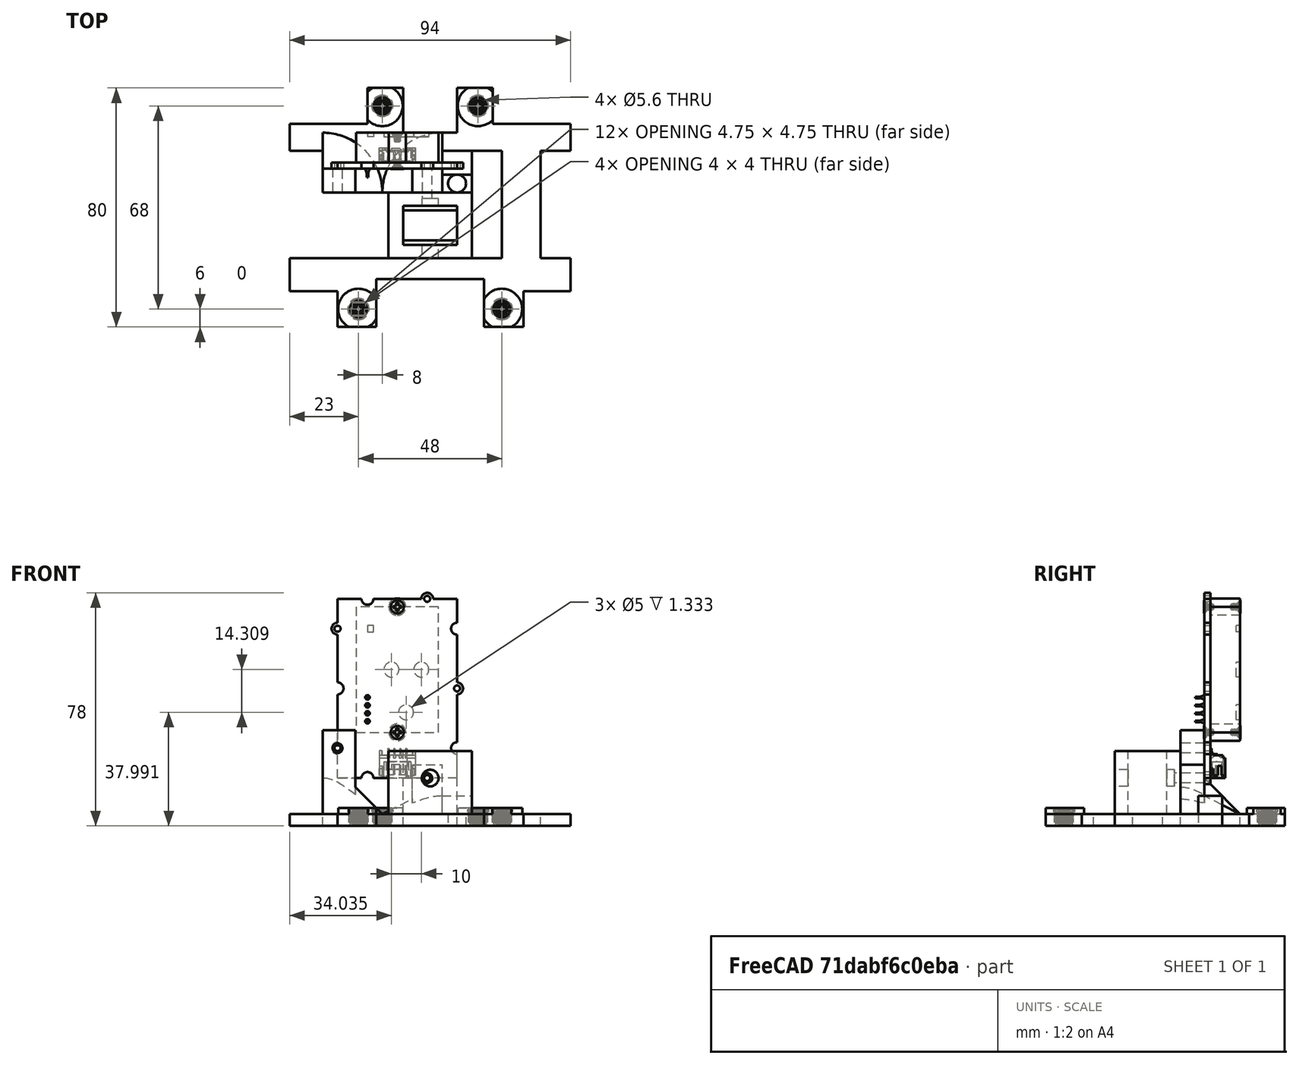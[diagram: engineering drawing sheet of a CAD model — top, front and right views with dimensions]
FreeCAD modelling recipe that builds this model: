
FCSTD DOCUMENT  (FreeCAD 0.20R29410 (Git))
Label: spin07132022
License: All rights reserved
LicenseURL: http://en.wikipedia.org/wiki/All_rights_reserved
objects: Part::Box×25, Part::Cylinder×18, Part::MultiFuse×16, Part::Cut×5, Part::Feature×5, Part::Cone×2
note: 71 computed .brp shape members not serialized (recipe doc carries the construction recipe); baked Part::Feature solids carry a one-line shape summary decoded from their .brp

FEATURE [Part::Cylinder] Cylinder103  label="Cylinder107"
  Angle = 360
  AttacherType = Attacher::AttachEngine3D
  FirstAngle = 0
  Height = 10
  Placement = pos=(63,3,0) rot=(0,0,1;0rad)
  Radius = 2.25
  SecondAngle = 0
FEATURE [Part::Box] Box064  label="base005"
  AttacherType = Attacher::AttachEngine3D
  Height = 4
  Length = 26
  Placement = pos=(-10.25,68,0) rot=(0,0,1;0rad)
  Width = 12
FEATURE [Part::Box] Box060  label="base001"
  AttacherType = Attacher::AttachEngine3D
  Height = 4
  Length = 94
  Width = 80
FEATURE [Part::Box] Box061  label="base002"
  AttacherType = Attacher::AttachEngine3D
  Height = 4
  Length = 26
  Width = 12
FEATURE [Part::Box] Box062  label="base003"
  AttacherType = Attacher::AttachEngine3D
  Height = 4
  Length = 26
  Placement = pos=(68,0,0) rot=(0,0,1;0rad)
  Width = 12
FEATURE [Part::Cylinder] Cylinder104  label="Cylinder103"
  Angle = 360
  AttacherType = Attacher::AttachEngine3D
  FirstAngle = 0
  Height = 10
  Placement = pos=(71,71,0) rot=(0,0,1;0rad)
  Radius = 2.25
  SecondAngle = 0
FEATURE [Part::Cylinder] Cylinder106  label="Cylinder104"
  Angle = 360
  AttacherType = Attacher::AttachEngine3D
  FirstAngle = 0
  Height = 10
  Placement = pos=(23,71,0) rot=(0,0,1;0rad)
  Radius = 2
  SecondAngle = 0
FEATURE [Part::Cylinder] Cylinder105  label="Cylinder108"
  Angle = 360
  AttacherType = Attacher::AttachEngine3D
  FirstAngle = 0
  Height = 10
  Placement = pos=(31,3,0) rot=(0,0,1;0rad)
  Radius = 2.25
  SecondAngle = 0
FEATURE [Part::Box] Box081  label="Cube039"
  AttacherType = Attacher::AttachEngine3D
  Height = 10
  Length = 10
  Placement = pos=(74,27,140) rot=(0,0,1;0rad)
  Width = 36
FEATURE [Part::Box] Box082  label="Cube040"
  AttacherType = Attacher::AttachEngine3D
  Height = 10
  Length = 36
  Placement = pos=(42,1,140) rot=(0,0,1;0rad)
  Width = 19
FEATURE [Part::Box] Box073  label="baseSpineCut"
  AttacherType = Attacher::AttachEngine3D
  Height = 25
  Length = 18
  Placement = pos=(51,33,140) rot=(0,0,1;0rad)
  Width = 10
FEATURE [Part::Cylinder] Cylinder107  label="Cylinder109"
  Angle = 360
  AttacherType = Attacher::AttachEngine3D
  FirstAngle = 0
  Height = 10
  Radius = 1
  SecondAngle = 0
FEATURE [Part::MultiFuse] Fusion123  label="screwIns001"
  Placement = pos=(0,3,0) rot=(0,0,1;0rad)
  Shapes = -> [Cylinder105,Cylinder107,Cylinder103,Cylinder104,Cylinder106]
FEATURE [Part::Box] Box080  label="Cube038"
  AttacherType = Attacher::AttachEngine3D
  Height = 10
  Length = 33
  Placement = pos=(13,27,140) rot=(0,0,1;0rad)
  Width = 22
FEATURE [Part::Box] Box063  label="base004"
  AttacherType = Attacher::AttachEngine3D
  Height = 4
  Length = 26
  Placement = pos=(78,68,0) rot=(0,0,1;0rad)
  Width = 12
FEATURE [Part::MultiFuse] Fusion122
  Shapes = -> [Box064,Box063,Box061,Box062]
FEATURE [Part::Cut] Cut019  label="baseNew"
  Base = -> Box060
  Tool = -> Fusion122
FEATURE [Part::Cut] Cut020  label="baseNew001"
  Base = -> Cut019
  Placement = pos=(107,84,140) rot=(0,0,1;3.14159rad)
  Tool = -> Fusion123
FEATURE [Part::Box] Box083  label="Cube041"
  AttacherType = Attacher::AttachEngine3D
  Height = 25
  Length = 18
  Placement = pos=(51,31.5,144) rot=(0,0,1;0rad)
  Width = 13
FEATURE [Part::Box] Box084  label="Cube042"
  AttacherType = Attacher::AttachEngine3D
  Height = 51
  Length = 50
  Placement = pos=(24,49,140) rot=(0,0,1;0rad)
  Width = 8
FEATURE [Part::Box] Box085  label="Cube043"
  AttacherType = Attacher::AttachEngine3D
  Height = 10
  Length = 15
  Placement = pos=(69,69,140) rot=(0,0,1;1.5708rad)
  Width = 18
FEATURE [Part::Box] Box086  label="baseSpineIn"
  AttacherType = Attacher::AttachEngine3D
  Height = 25
  Length = 28
  Placement = pos=(46,27,140) rot=(0,0,1;0rad)
  Width = 22
FEATURE [Part::Cylinder] Cylinder
  Angle = 360
  AttacherType = Attacher::AttachEngine3D
  FirstAngle = 0
  Height = 50
  Placement = pos=(60,-3,156) rot=(-1,0,0;1.5708rad)
  Radius = 2.8
  SecondAngle = 0
FEATURE [Part::Feature] Feature  label="Seed Grove SCD30"
  Placement = pos=(29,59,156) rot=(0.707107,0,0.707107;3.14159rad)
  shape: bbox 44 x 15.1 x 64 mm, 422 faces, 13 solids (baked)
FEATURE [Part::Cylinder] Cylinder108  label="Cylinder110"
  Angle = 360
  AttacherType = Attacher::AttachEngine3D
  FirstAngle = 0
  Height = 50
  Placement = pos=(80,17,186) rot=(-1,0,0;1.5708rad)
  Radius = 1.65
  SecondAngle = 0
FEATURE [Part::Cylinder] Cylinder109  label="Cylinder111"
  Angle = 360
  AttacherType = Attacher::AttachEngine3D
  FirstAngle = 0
  Height = 50
  Placement = pos=(40,17,166) rot=(-1,0,0;1.5708rad)
  Radius = 1.65
  SecondAngle = 0
FEATURE [Part::Cylinder] Cylinder110  label="Cylinder112"
  Angle = 360
  AttacherType = Attacher::AttachEngine3D
  FirstAngle = 0
  Height = 50
  Placement = pos=(70,17,156) rot=(-1,0,0;1.5708rad)
  Radius = 1.65
  SecondAngle = 0
FEATURE [Part::MultiFuse] Fusion  label="m2Cuts"
  Placement = pos=(-11,30,0) rot=(0,0,1;0rad)
  Shapes = -> [Cylinder108,Cylinder109,Cylinder110]
FEATURE [Part::Box] Box087  label="Cube044"
  AttacherType = Attacher::AttachEngine3D
  Height = 51
  Length = 50
  Placement = pos=(13,49,172) rot=(0,0,1;0rad)
  Width = 8
FEATURE [Part::Box] Box088  label="Cube045"
  AttacherType = Attacher::AttachEngine3D
  Height = 51
  Length = 19
  Placement = pos=(35,49,144) rot=(0,0,1;0rad)
  Width = 8
FEATURE [Part::MultiFuse] Fusion124  label="base"
  Shapes = -> [Cut020,Box084,Box086]
FEATURE [Part::MultiFuse] Fusion125  label="cuts"
  Shapes = -> [Box087,Box088,Fusion,Box085,Box080,Box083,Box082,Box081,Box073,Cylinder]
FEATURE [Part::Box] Box089  label="Cube046"
  AttacherType = Attacher::AttachEngine3D
  Height = 10
  Length = 11
  Placement = pos=(13,57,140) rot=(0,0,1;0rad)
  Width = 6
FEATURE [Part::Feature] Solid  label="m4HeatSet"
  Placement = pos=(36,10,140) rot=(1,0,0;1.5708rad)
  shape: bbox 7.1 x 7.1 x 6.065 mm, 234 faces (baked)
FEATURE [Part::Feature] Solid001  label="m4HeatSet001"
  Placement = pos=(84,10,140) rot=(1,0,0;1.5708rad)
  shape: bbox 7.1 x 7.1 x 6.065 mm, 234 faces (baked)
FEATURE [Part::Feature] Solid002  label="m4HeatSet002"
  Placement = pos=(44,78,140) rot=(1,0,0;1.5708rad)
  shape: bbox 7.1 x 7.1 x 6.065 mm, 234 faces (baked)
FEATURE [Part::Feature] Solid003  label="m4HeatSet003"
  Placement = pos=(76,78,140) rot=(1,0,0;1.5708rad)
  shape: bbox 7.1 x 7.1 x 6.065 mm, 234 faces (baked)
FEATURE [Part::Cylinder] Cylinder111  label="m4HeatSetCut"
  Angle = 360
  AttacherType = Attacher::AttachEngine3D
  FirstAngle = 0
  Height = 10
  Placement = pos=(36,10,140) rot=(0,0,1;0rad)
  Radius = 2.8
  SecondAngle = 0
FEATURE [Part::Cylinder] Cylinder112  label="m4HeatSetCut001"
  Angle = 360
  AttacherType = Attacher::AttachEngine3D
  FirstAngle = 0
  Height = 10
  Placement = pos=(84,10,140) rot=(0,0,1;0rad)
  Radius = 2.8
  SecondAngle = 0
FEATURE [Part::Cylinder] Cylinder113  label="m4HeatSetCut002"
  Angle = 360
  AttacherType = Attacher::AttachEngine3D
  FirstAngle = 0
  Height = 10
  Placement = pos=(76,78,140) rot=(0,0,1;0rad)
  Radius = 2.8
  SecondAngle = 0
FEATURE [Part::Cylinder] Cylinder114  label="m4HeatSetCut003"
  Angle = 360
  AttacherType = Attacher::AttachEngine3D
  FirstAngle = 0
  Height = 10
  Placement = pos=(44,78,140) rot=(0,0,1;0rad)
  Radius = 2.8
  SecondAngle = 0
FEATURE [Part::MultiFuse] Fusion126  label="heatSetCuts"
  Shapes = -> [Cylinder111,Cylinder112,Cylinder113,Cylinder114]
FEATURE [Part::Box] Box091  label="Cube048"
  AttacherType = Attacher::AttachEngine3D
  Height = 10
  Length = 11
  Placement = pos=(13,49,140) rot=(0,0,1;0rad)
  Width = 8
FEATURE [Part::MultiFuse] Fusion127  label="cuts001"
  Shapes = -> [Box091,Fusion126,Box089,Fusion125]
FEATURE [Part::Cylinder] Cylinder115  label="m4HeatSetCut004"
  Angle = 360
  AttacherType = Attacher::AttachEngine3D
  FirstAngle = 0
  Height = 6
  Placement = pos=(36,10,140) rot=(0,0,-1;1.0472rad)
  Radius = 6.8
  SecondAngle = 0
FEATURE [Part::Cylinder] Cylinder116  label="m4HeatSetCut005"
  Angle = 360
  AttacherType = Attacher::AttachEngine3D
  FirstAngle = 0
  Height = 6
  Placement = pos=(84,10,140) rot=(0,0,1;0rad)
  Radius = 6.8
  SecondAngle = 0
FEATURE [Part::Cylinder] Cylinder117  label="m4HeatSetCut006"
  Angle = 360
  AttacherType = Attacher::AttachEngine3D
  FirstAngle = 0
  Height = 6
  Placement = pos=(76,78,140) rot=(0,0,1;0rad)
  Radius = 6.8
  SecondAngle = 0
FEATURE [Part::Cylinder] Cylinder118  label="m4HeatSetCut007"
  Angle = 360
  AttacherType = Attacher::AttachEngine3D
  FirstAngle = 0
  Height = 6
  Placement = pos=(44,78,140) rot=(0,0,1;0rad)
  Radius = 6.8
  SecondAngle = 0
FEATURE [Part::MultiFuse] Fusion128  label="heatSetAddOns"
  Shapes = -> [Cylinder115,Cylinder116,Cylinder117,Cylinder118]
FEATURE [Part::Box] Box092  label="Cube049"
  AttacherType = Attacher::AttachEngine3D
  Height = 10
  Length = 94
  Placement = pos=(13,-4,140) rot=(0,0,1;0rad)
  Width = 8
FEATURE [Part::MultiFuse] Fusion129  label="base006"
  Shapes = -> [Fusion128,Fusion124]
FEATURE [Part::Box] Box093  label="Cube050"
  AttacherType = Attacher::AttachEngine3D
  Height = 10
  Length = 94
  Placement = pos=(13,84,140) rot=(0,0,1;0rad)
  Width = 8
FEATURE [Part::Box] Box094  label="Cube051"
  AttacherType = Attacher::AttachEngine3D
  Height = 10
  Length = 94
  Placement = pos=(89,72,140) rot=(0,0,1;1.5708rad)
  Width = 8
FEATURE [Part::Box] Box095  label="Cube052"
  AttacherType = Attacher::AttachEngine3D
  Height = 10
  Length = 94
  Placement = pos=(39,72,140) rot=(0,0,1;1.5708rad)
  Width = 8
FEATURE [Part::MultiFuse] Fusion130
  Shapes = -> [Box093,Box094,Box095,Box092]
FEATURE [Part::MultiFuse] Fusion131  label="cuts002"
  Shapes = -> [Fusion127,Fusion130]
FEATURE [Part::Box] Box096  label="Cube053"
  AttacherType = Attacher::AttachEngine3D
  Height = 10
  Length = 10
  Placement = pos=(97,27,140) rot=(0,0,1;0rad)
  Width = 36
FEATURE [Part::MultiFuse] Fusion132  label="cuts003"
  Shapes = -> [Fusion131,Box096]
FEATURE [Part::Cut] Cut  label="base007"
  Base = -> Fusion129
  Tool = -> Fusion132
FEATURE [Part::Cone] Cone
  Angle = 90
  AttacherType = Attacher::AttachEngine3D
  Height = 12
  Placement = pos=(24,49,144) rot=(0,0,1;0rad)
  Radius1 = 20
  Radius2 = 8
FEATURE [Part::Box] Box  label="Cube"
  AttacherType = Attacher::AttachEngine3D
  Height = 60
  Length = 11
  Placement = pos=(64,49,144) rot=(0,0,1;0rad)
  Width = 8
FEATURE [Part::Box] Box097  label="Cube054"
  AttacherType = Attacher::AttachEngine3D
  Height = 55
  Length = 11
  Placement = pos=(54,49,160.5) rot=(0,0,1;0rad)
  Width = 8
FEATURE [Part::MultiFuse] Fusion133  label="cuts004"
  Shapes = -> [Box,Box097]
FEATURE [Part::Cut] Cut021
  Base = -> Cut
  Tool = -> Fusion133
FEATURE [Part::Cylinder] Cylinder119  label="m4HeatSetCut008"
  Angle = 360
  AttacherType = Attacher::AttachEngine3D
  FirstAngle = 0
  Height = 10
  Placement = pos=(69,52,140) rot=(0,0,1;0rad)
  Radius = 3
  SecondAngle = 0
FEATURE [Part::MultiFuse] Fusion134
  Shapes = -> [Cone,Cut021]
FEATURE [Part::Cut] Cut022
  Base = -> Fusion134
  Tool = -> Cylinder119
FEATURE [Part::Box] Box098  label="Cube055"
  AttacherType = Attacher::AttachEngine3D
  Height = 10
  Length = 10
  Placement = pos=(64,55,140) rot=(0,0,1;0rad)
  Width = 8
FEATURE [Part::MultiFuse] Fusion135
  Shapes = -> [Cut022,Box098]
FEATURE [Part::Cone] Cone001
  Angle = 90
  AttacherType = Attacher::AttachEngine3D
  Height = 6
  Placement = pos=(64,49,144) rot=(0,0,1;1.5708rad)
  Radius1 = 20
  Radius2 = 8
FEATURE [Part::MultiFuse] Fusion136
  Shapes = -> [Fusion135,Cone001]
